# Revit family: QF_BPRO_BC PC 4800_574210
name_source: partatom
category: Sonderausstattung
revit_build: Autodesk Revit 2018 (Build: 20190510_1515(x64)
units: mm (PartAtom-declared; Revit-internal decimal feet)

## family parameters
Arbeitsebenenbasiert = Nein
Beim Laden mit Abzugskörper schneiden = Nein
Bemaßung runder Anschluss = Durchmesser verwenden
Gemeinsam genutzt = Nein
Immer vertikal = Ja
Raumberechnungspunkt = Ja
Teiletyp = Normal

## types (1)
- BC PC 4800
    Artikel Nummer = 574210
    Becken Länge = 305 mm  [stored 1.00066 ft]
    Becken Tiefe = 506 mm
    Becken Versatz von vorne = 58 mm
    Beckentiefe = 165 mm  [stored 0.541339 ft]
    Beschreibung = Pastakocher für GN Behälter oder Pastakörben
    Beschreibung durch Hersteller analog Leistungsverzeichniskurztext = BC PC 4800
Pastakocher
nahtlos tiefgezogenes
Becken, für die Aufnahme von
GN-Behälter oder
Pastakörben bis
150 mm Tiefe,
Kontrollleuchte zur Anzeige
des Betriebszustands und der
Aufheizphase
    Beschreibung durch Hersteller analog Leistungsverzeichnislangtext = BC PC 4800
Pastakocher
nahtlos tiefgezogenes
Becken, für die Aufnahme von
GN-Behälter oder
Pastakörben bis
150 mm Tiefe,
Kontrollleuchte zur Anzeige
des Betriebszustands und der
Aufheizphase
    CE Kennzeichnung = Ja
    Elektrische leistung = 4800 W
    Frequenz = 50 Hz
    Gerätegewicht Netto = 14.00 kg
    Großküchengerätezuordnung = Ja
    Hauptschalter integriert = Ja
    Hersteller = B.PRO GmbH
    Höhe = 240 mm
    Internetadresse Gerätehersteller = https://www.bpro-solutions.com
    Internetadresse für Ersatzteilliste = https://www.bpro-solutions.com
    Kosten = 2634 $
    Länge Gerätebreite = 400 mm
    Material = QF_Metal-Stainless-Steel_general
    Modell = BC PC 4800
    Phasen = 3
    Spannung = 400 V
    Tiefe = 620 mm
    Typenkommentare = Pastakocher BC PC 4800
    URL = https://www.bpro-solutions.com
    Zubehör = Ja
    Zuleitung zum Gerät im Lieferumfang = Ja

note: [stored X ft] marks values corroborated as IEEE doubles in the binary element streams (Revit-internal decimal feet)
